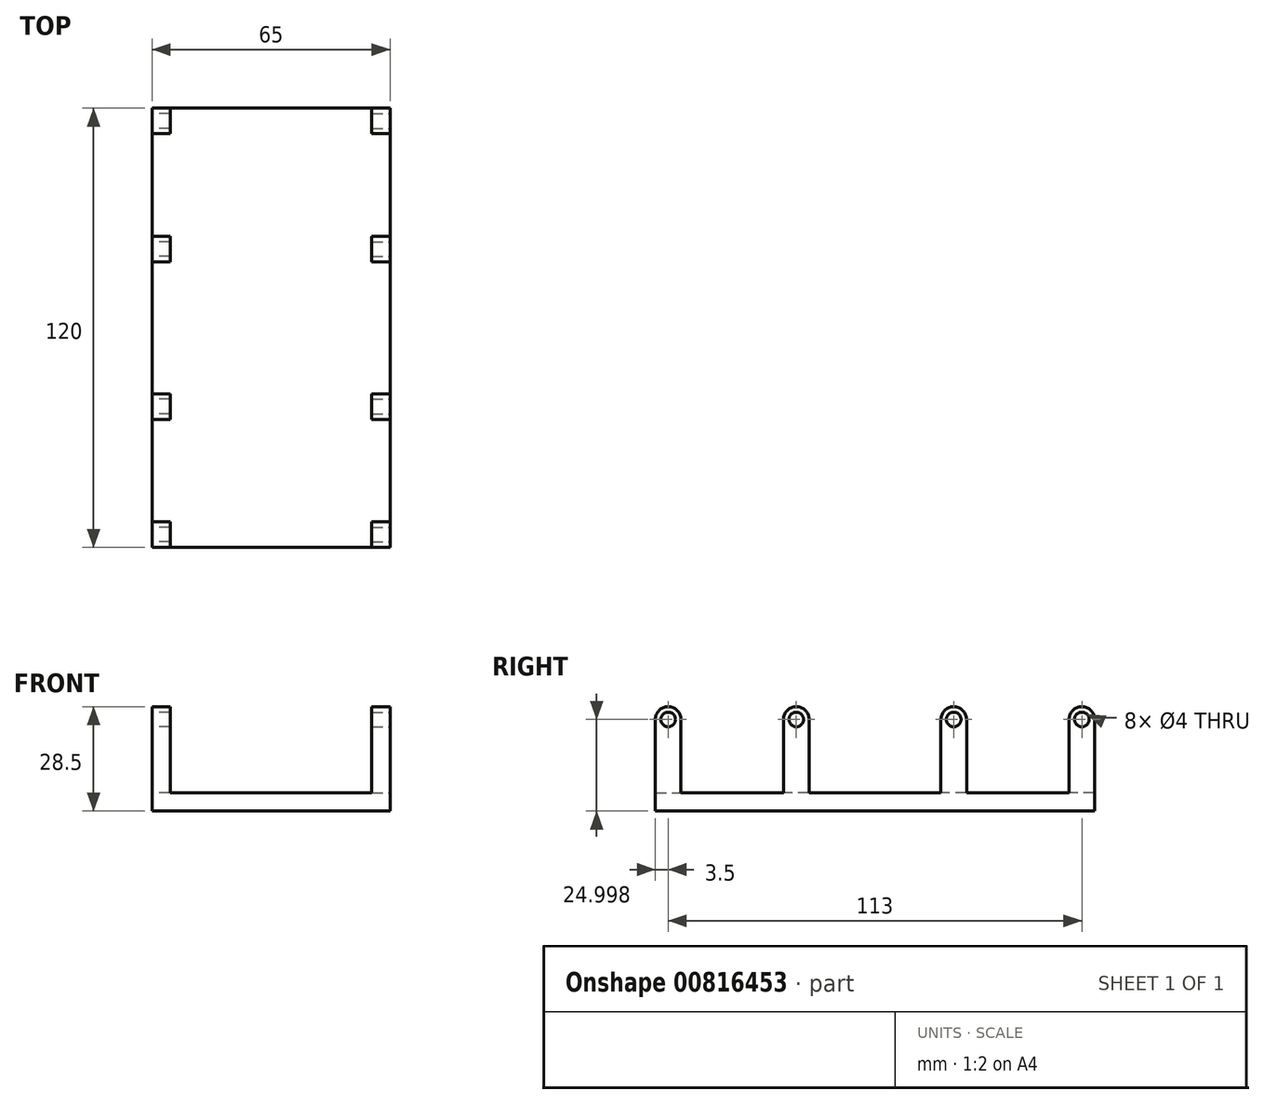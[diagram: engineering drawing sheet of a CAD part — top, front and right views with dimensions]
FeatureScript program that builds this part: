
annotation { "Feature Type Name" : "Feature", "Feature Type Description" : "" }
export const myFeature = defineFeature(function(context is Context, id is Id, definition is map)
    precondition{}
    {
        {
            var Q0;
            Q0=qCreatedBy(makeId("Right.planeOp"),FACE);
            var sketch = newSketch(context, id + "F0", { "sketchPlane" : qUnion([Q0])});
            skArc(sketch, "E0", {"start": v(-17.5, 1.78) * mm, "mid": v(-19.97, 0.75) * mm, "end": v(-21, -1.72) * mm});
            skArc(sketch, "E1", {"start": v(17.5, 1.78) * mm, "mid": v(19.97, 0.75) * mm, "end": v(21, -1.72) * mm});
            skPoint(sketch, "E2", {"position": v(-21, -1.72) * mm});
            skPoint(sketch, "E3", {"position": v(21, -1.72) * mm});
            skLineSegment(sketch, "E4", {"start": v(-14, -1.72) * mm, "end": v(14, -1.72) * mm, "construction": true});
            skArc(sketch, "E5", {"start": v(-14, -1.72) * mm, "mid": v(-17.5, 1.78) * mm, "end": v(-21, -1.72) * mm, "construction": true});
            skPoint(sketch, "E6", {"position": v(-14, -1.72) * mm});
            skLineSegment(sketch, "E7.top", {"start": v(-21, -21.72) * mm, "end": v(-14, -21.72) * mm});
            skLineSegment(sketch, "E7.left", {"start": v(-21, -1.72) * mm, "end": v(-21, -21.72) * mm});
            skLineSegment(sketch, "E7.right", {"start": v(-14, -5.22) * mm, "end": v(-14, -21.72) * mm});
            skLineSegment(sketch, "E8", {"start": v(0, -20.25) * mm, "end": v(0, 46.56) * mm, "construction": true});
            skLineSegment(sketch, "E9.MirrorCS", {"start": v(14, -5.22) * mm, "end": v(14, -21.72) * mm});
            skLineSegment(sketch, "E10.MirrorCS", {"start": v(21, -21.72) * mm, "end": v(14, -21.72) * mm});
            skLineSegment(sketch, "E11.MirrorCS", {"start": v(21, -1.72) * mm, "end": v(21, -21.72) * mm});
            skArc(sketch, "E12.MirrorCS", {"start": v(14, -1.72) * mm, "mid": v(17.5, 1.78) * mm, "end": v(21, -1.72) * mm, "construction": true});
            skLineSegment(sketch, "E13.trimOffspring", {"start": v(17.5, -1.72) * mm, "end": v(21, -1.72) * mm, "construction": true});
            skPoint(sketch, "E14.end.orphan", {"position": v(0, 1.78) * mm});
            skLineSegment(sketch, "E15", {"start": v(-14, -5.22) * mm, "end": v(-14, -1.72) * mm});
            skLineSegment(sketch, "E16", {"start": v(14, -5.22) * mm, "end": v(14, -1.72) * mm});
            skArc(sketch, "E17", {"start": v(-14, -1.72) * mm, "mid": v(-17.5, 1.78) * mm, "end": v(-21, -1.72) * mm});
            skArc(sketch, "E18", {"start": v(21, -1.72) * mm, "mid": v(17.5, 1.78) * mm, "end": v(14, -1.72) * mm});
            skCircle(sketch, "E19", {"center": v(-17.5, -1.72) * mm, "radius": 2 * mm});
            skCircle(sketch, "E20.MirrorC", {"center": v(17.5, -1.72) * mm, "radius": 2 * mm});
            skLineSegment(sketch, "E21", {"start": v(-21, -21.72) * mm, "end": v(39, -21.72) * mm, "construction": true});
            skLineSegment(sketch, "E22", {"start": v(39, -21.72) * mm, "end": v(39, 0) * mm, "construction": true});
            skLineSegment(sketch, "E23.MirrorCS", {"start": v(57, -1.72) * mm, "end": v(57, -21.72) * mm});
            skLineSegment(sketch, "E24.MirrorCS", {"start": v(64, -5.22) * mm, "end": v(64, -21.72) * mm});
            skLineSegment(sketch, "E25.MirrorCS", {"start": v(64, -5.22) * mm, "end": v(64, -1.72) * mm});
            skCircle(sketch, "E26.MirrorC", {"center": v(60.5, -1.72) * mm, "radius": 2 * mm});
            skArc(sketch, "E27.MirrorCS", {"start": v(64, -1.72) * mm, "mid": v(60.5, 1.78) * mm, "end": v(57, -1.72) * mm});
            skArc(sketch, "E28.MirrorCS", {"start": v(64, -1.72) * mm, "mid": v(60.5, 1.78) * mm, "end": v(57, -1.72) * mm, "construction": true});
            skLineSegment(sketch, "E29.MirrorCS", {"start": v(92, -5.22) * mm, "end": v(92, -21.72) * mm});
            skLineSegment(sketch, "E30.MirrorCS", {"start": v(92, -5.22) * mm, "end": v(92, -1.72) * mm});
            skLineSegment(sketch, "E31.MirrorCS", {"start": v(99, -1.72) * mm, "end": v(99, -21.72) * mm});
            skCircle(sketch, "E32.MirrorC", {"center": v(95.5, -1.72) * mm, "radius": 2 * mm});
            skArc(sketch, "E33.MirrorCS", {"start": v(92, -1.72) * mm, "mid": v(95.5, 1.78) * mm, "end": v(99, -1.72) * mm});
            skLineSegment(sketch, "E34.MirrorCS", {"start": v(99, -21.72) * mm, "end": v(92, -21.72) * mm});
            skLineSegment(sketch, "E35.trimOffspring", {"start": v(64, -21.72) * mm, "end": v(57, -21.72) * mm});
            skPoint(sketch, "E36.orphan", {"position": v(39, -21.72) * mm});
            skSolve(sketch);
        }
        {
            var Q0;
            Q0 = qSketchRegion(id + "F0", true);
            extrude(context, id + "F1", {"entities" : qUnion([Q0]), "depth" : 5 * mm, "offsetDistance" : 25 * mm});
        }
        {
            var Q0;
            Q0=makeQuery(id+"F1.opExtrude","SWEPT_FACE",FACE,{"disambiguationData":[OSD([sQuery(id+"F0.wireOp",EDGE,"E7.top")])]});
            var sketch = newSketch(context, id + "F2", { "sketchPlane" : qUnion([Q0])});
            skLineSegment(sketch, "E37.bottom", {"start": v(0, 21) * mm, "end": v(60, 21) * mm});
            skLineSegment(sketch, "E37.top", {"start": v(0, -99) * mm, "end": v(60, -99) * mm});
            skLineSegment(sketch, "E37.left", {"start": v(0, 21) * mm, "end": v(0, -99) * mm});
            skLineSegment(sketch, "E37.right", {"start": v(60, 21) * mm, "end": v(60, -99) * mm});
            skSolve(sketch);
        }
        {
            var Q0;
            {var subQ3=sQuery(id+"F2.wireOp",EDGE,"E37.top");Q0=makeQuery(id+"F2.imprint","IMPRINT",FACE,{"disambiguationData":[TD([[makeQuery(id+"F2.imprint","IMPRINT",EDGE,{"derivedFrom":subQ3}),1.0]])]});}
            var Q1;
            {var subQ3=sQuery(id+"F0.wireOp",EDGE,"E7.top");var subQ4=makeQuery(id+"F1.opExtrude","CAP_EDGE",EDGE,{"disambiguationData":[OSD([subQ3])],"isStart":false});Q1=makeQuery(id+"F2.imprint","IMPRINT",FACE,{"disambiguationData":[TD([[makeQuery(id+"F2.imprint","IMPRINT",EDGE,{"derivedFrom":subQ4}),-1.0]])]});}
            extrude(context, id + "F3", {"entities" : qUnion([Q0, Q1]), "operationType" : NewBodyOperationType.ADD, "depth" : 5 * mm, "offsetDistance" : 25 * mm});
        }
        {
            var Q0;
            Q0=makeQuery(id+"F3.boolean.opBoolean","MERGE",FACE,{"derivedFrom":[makeQuery(id+"F1.opExtrude","SWEPT_FACE",FACE,{"disambiguationData":[OSD([sQuery(id+"F0.wireOp",EDGE,"E7.left")])]}),makeQuery(id+"F3.opExtrude","SWEPT_FACE",FACE,{"disambiguationData":[OSD([sQuery(id+"F2.wireOp",EDGE,"E37.bottom")])]})]});
            var sketch = newSketch(context, id + "F4", { "sketchPlane" : qUnion([Q0])});
            skLineSegment(sketch, "E38", {"start": v(32.5, -21.72) * mm, "end": v(32.5, -26.72) * mm, "construction": true});
            skSolve(sketch);
        }
        {
            var Q0;
            Q0=makeQuery(id+"F3.opExtrude","CAP_EDGE",EDGE,{"disambiguationData":[OSD([sQuery(id+"F2.wireOp",EDGE,"E37.top")])],"isStart":true});
            cPoint(context, id + "F5", {"entities" : qUnion([Q0]), "parameter" : 0.5});
        }
        {
            var Q0;
            Q0=sQuery(id+"F4.wireOp",VERTEX,"E38.start");
            var Q1;
            Q1=sQuery(id+"F4.wireOp",VERTEX,"E38.end");
            var Q2;
            Q2 = qCreatedBy(id + "F5" ,VERTEX);
            cPlane(context, id + "F6", {"entities" : qUnion([Q0, Q1, Q2]), "cplaneType" : CPlaneType.THREE_POINT, "offset" : 25 * mm, "width" : 150 * mm, "height" : 150 * mm});
        }
        {
            var Q0;
            Q0=makeQuery(id+"F1.opExtrude","SWEPT_BODY",BODY,{"disambiguationData":[OSD([sQuery(id+"F0.wireOp",EDGE,"E7.top"),sQuery(id+"F0.wireOp",EDGE,"E7.left"),sQuery(id+"F0.wireOp",EDGE,"E7.right"),sQuery(id+"F0.wireOp",EDGE,"E15"),sQuery(id+"F0.wireOp",EDGE,"E17"),sQuery(id+"F0.wireOp",EDGE,"E19")])]});
            var Q1;
            Q1=qCreatedBy(id+"F6.planeOp",FACE);
            mirror(context, id + "F7", {"operationType" : NewBodyOperationType.ADD, "entities" : qUnion([Q0]), "mirrorPlane" : qUnion([Q1])});
        }
    });
